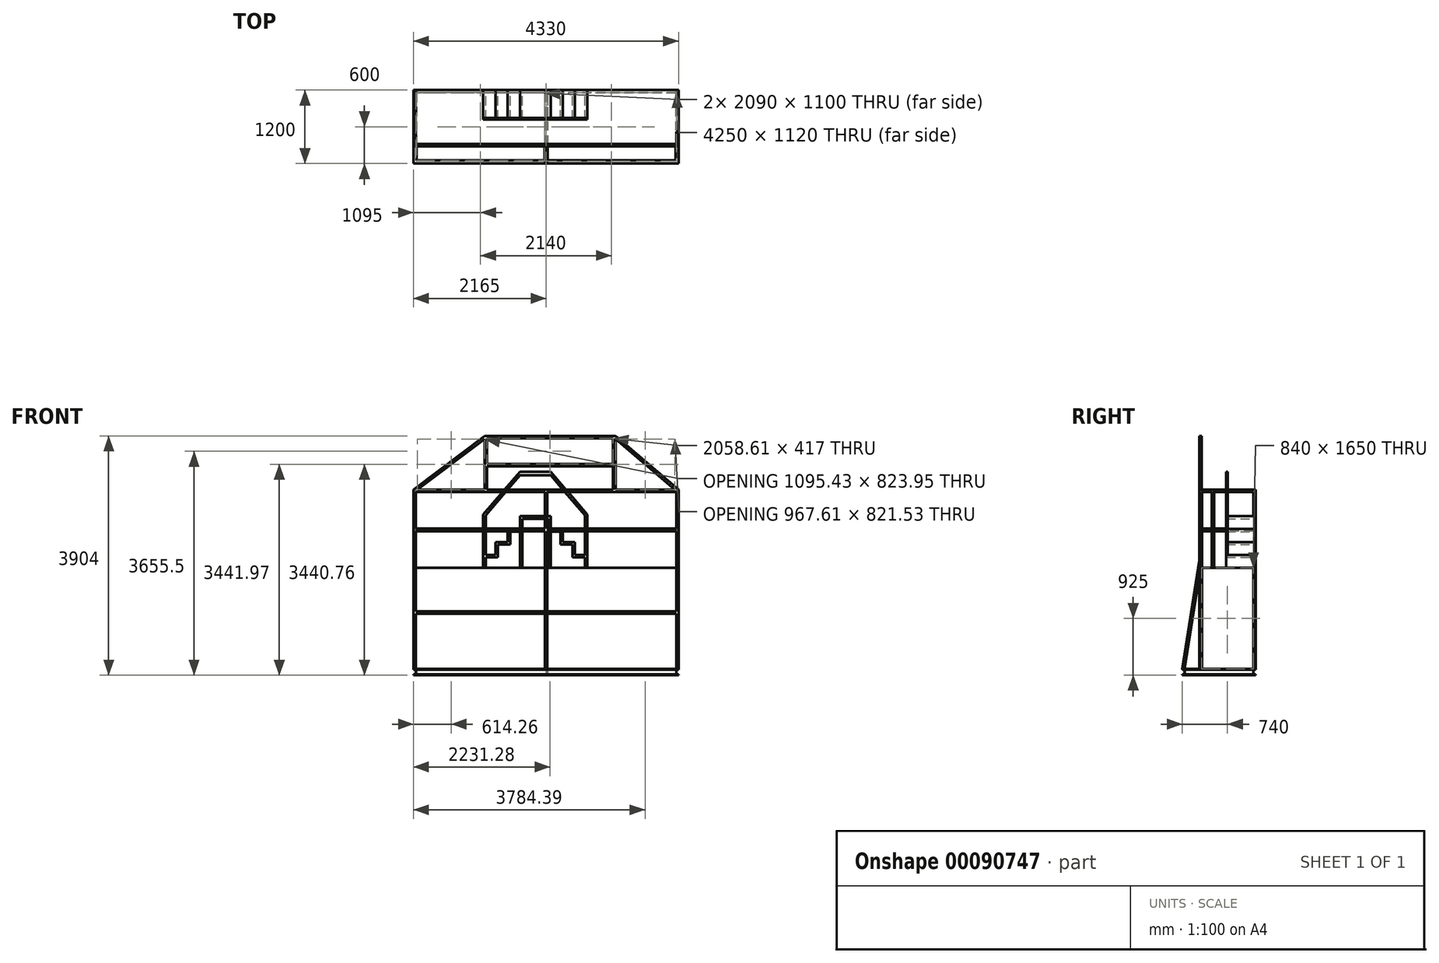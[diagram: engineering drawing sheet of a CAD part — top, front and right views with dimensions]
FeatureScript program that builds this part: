
annotation { "Feature Type Name" : "Feature", "Feature Type Description" : "" }
export const myFeature = defineFeature(function(context is Context, id is Id, definition is map)
    precondition{}
    {
        {
            var Q0;
            Q0=qCreatedBy(makeId("Top.planeOp"),FACE);
            var sketch = newSketch(context, id + "F0", { "sketchPlane" : qUnion([Q0])});
            skLineSegment(sketch, "E0.rect.bottom", {"start": v(2165, 600) * mm, "end": v(-2165, 600) * mm});
            skLineSegment(sketch, "E0.rect.top", {"start": v(2165, -600) * mm, "end": v(-2165, -600) * mm});
            skLineSegment(sketch, "E0.rect.left", {"start": v(2165, 600) * mm, "end": v(2165, -600) * mm});
            skLineSegment(sketch, "E0.rect.right", {"start": v(-2165, 600) * mm, "end": v(-2165, -600) * mm});
            skPoint(sketch, "E0.rect.middle", {"position": v(0, 0) * mm});
            skLineSegment(sketch, "E1.rect.bottom", {"start": v(2115, 550) * mm, "end": v(25, 550) * mm});
            skLineSegment(sketch, "E1.rect.top", {"start": v(2115, -550) * mm, "end": v(25, -550) * mm});
            skLineSegment(sketch, "E1.rect.left", {"start": v(2115, 550) * mm, "end": v(2115, -550) * mm});
            skLineSegment(sketch, "E1.rect.right", {"start": v(-2115, 550) * mm, "end": v(-2115, -550) * mm});
            skLineSegment(sketch, "E2.rect.left", {"start": v(25, 550) * mm, "end": v(25, -550) * mm});
            skLineSegment(sketch, "E2.rect.right", {"start": v(-25, 550) * mm, "end": v(-25, -550) * mm});
            skLineSegment(sketch, "E3.trimOffspring", {"start": v(-25, 550) * mm, "end": v(-2115, 550) * mm});
            skLineSegment(sketch, "E4.trimOffspring", {"start": v(-25, -550) * mm, "end": v(-2115, -550) * mm});
            skSolve(sketch);
        }
        {
            var Q0;
            Q0=makeQuery(id+"F0.imprint","IMPRINT",FACE,{"disambiguationData":[TD([[makeQuery(id+"F0.imprint","IMPRINT",EDGE,{"derivedFrom":sQuery(id+"F0.wireOp",EDGE,"E0.rect.bottom")}),1.0]])]});
            extrude(context, id + "F1", {"entities" : qUnion([Q0]), "depth" : 100 * mm});
        }
        {
            var Q0;
            Q0=makeQuery(id+"F1.opExtrude","SWEPT_FACE",FACE,{"disambiguationData":[OSD([sQuery(id+"F0.wireOp",EDGE,"E0.rect.right")])]});
            var sketch = newSketch(context, id + "F2", { "sketchPlane" : qUnion([Q0])});
            skLineSegment(sketch, "E5.bottom", {"start": v(-600, 90) * mm, "end": v(-560, 90) * mm});
            skLineSegment(sketch, "E5.top", {"start": v(-600, 10) * mm, "end": v(-560, 10) * mm});
            skLineSegment(sketch, "E5.left", {"start": v(-600, 90) * mm, "end": v(-600, 10) * mm});
            skLineSegment(sketch, "E5.right", {"start": v(-560, 90) * mm, "end": v(-560, 10) * mm});
            skLineSegment(sketch, "E6.bottom", {"start": v(600, 90) * mm, "end": v(560, 90) * mm});
            skLineSegment(sketch, "E6.top", {"start": v(600, 10) * mm, "end": v(560, 10) * mm});
            skLineSegment(sketch, "E6.left", {"start": v(600, 90) * mm, "end": v(600, 10) * mm});
            skLineSegment(sketch, "E6.right", {"start": v(560, 90) * mm, "end": v(560, 10) * mm});
            skSolve(sketch);
        }
        {
            var Q0;
            Q0=makeQuery(id+"F2.imprint","IMPRINT",FACE,{"disambiguationData":[TD([[makeQuery(id+"F2.imprint","IMPRINT",EDGE,{"derivedFrom":sQuery(id+"F2.wireOp",EDGE,"E5.bottom")}),-1.0]])]});
            var Q1;
            Q1=makeQuery(id+"F2.imprint","IMPRINT",FACE,{"disambiguationData":[TD([[makeQuery(id+"F2.imprint","IMPRINT",EDGE,{"derivedFrom":sQuery(id+"F2.wireOp",EDGE,"E6.bottom")}),1.0]])]});
            extrude(context, id + "F3", {"entities" : qUnion([Q0, Q1]), "operationType" : NewBodyOperationType.REMOVE, "endBound" : BoundingType.THROUGH_ALL, "oppositeDirection" : true, "depth" : 25 * mm});
        }
        {
            var Q0;
            Q0=makeQuery(id+"F3.boolean.opBoolean","COPY",FACE,{"derivedFrom":makeQuery(id+"F3.opExtrude","SWEPT_FACE",FACE,{"disambiguationData":[OSD([sQuery(id+"F2.wireOp",EDGE,"E6.right")])]})});
            var sketch = newSketch(context, id + "F4", { "sketchPlane" : qUnion([Q0])});
            skLineSegment(sketch, "E7.bottom", {"start": v(2165, 90) * mm, "end": v(2125, 90) * mm});
            skLineSegment(sketch, "E7.top", {"start": v(2165, 10) * mm, "end": v(2125, 10) * mm});
            skLineSegment(sketch, "E7.left", {"start": v(2165, 90) * mm, "end": v(2165, 10) * mm});
            skLineSegment(sketch, "E7.right", {"start": v(2125, 90) * mm, "end": v(2125, 10) * mm});
            skLineSegment(sketch, "E8.bottom", {"start": v(-2165, 90) * mm, "end": v(-2125, 90) * mm});
            skLineSegment(sketch, "E8.top", {"start": v(-2165, 10) * mm, "end": v(-2125, 10) * mm});
            skLineSegment(sketch, "E8.left", {"start": v(-2165, 90) * mm, "end": v(-2165, 10) * mm});
            skLineSegment(sketch, "E8.right", {"start": v(-2125, 90) * mm, "end": v(-2125, 10) * mm});
            skSolve(sketch);
        }
        {
            var Q0;
            Q0=makeQuery(id+"F4.imprint","IMPRINT",FACE,{"disambiguationData":[TD([[makeQuery(id+"F4.imprint","IMPRINT",EDGE,{"derivedFrom":sQuery(id+"F4.wireOp",EDGE,"E7.bottom")}),1.0]])]});
            var Q1;
            Q1=makeQuery(id+"F4.imprint","IMPRINT",FACE,{"disambiguationData":[TD([[makeQuery(id+"F4.imprint","IMPRINT",EDGE,{"derivedFrom":sQuery(id+"F4.wireOp",EDGE,"E8.bottom")}),1.0]])]});
            extrude(context, id + "F5", {"entities" : qUnion([Q0, Q1]), "operationType" : NewBodyOperationType.REMOVE, "endBound" : BoundingType.THROUGH_ALL, "oppositeDirection" : true, "depth" : 25 * mm});
        }
        {
            var Q0;
            Q0=qCreatedBy(makeId("Top.planeOp"),FACE);
            cPlane(context, id + "F6", {"entities" : qUnion([Q0]), "cplaneType" : CPlaneType.OFFSET, "offset" : 1750 * mm, "width" : 150 * mm, "height" : 150 * mm});
        }
        {
            var Q0;
            Q0=qCreatedBy(makeId("Front.planeOp"),FACE);
            var sketch = newSketch(context, id + "F7", { "sketchPlane" : qUnion([Q0])});
            skLineSegment(sketch, "E9.bottom", {"start": v(0, 10) * mm, "end": v(-90, 10) * mm});
            skLineSegment(sketch, "E9.top", {"start": v(0, 90) * mm, "end": v(-90, 90) * mm});
            skLineSegment(sketch, "E9.left", {"start": v(0, 10) * mm, "end": v(0, 90) * mm});
            skLineSegment(sketch, "E9.right", {"start": v(-90, 10) * mm, "end": v(-90, 90) * mm});
            skSolve(sketch);
        }
        {
            var Q0;
            Q0=qSketchRegion(id+"F7",true);
            var Q1;
            Q1=makeQuery(id+"F1.opExtrude","SWEPT_FACE",FACE,{"disambiguationData":[OSD([sQuery(id+"F0.wireOp",EDGE,"E3.trimOffspring")])]});
            var Q2;
            Q2=makeQuery(id+"F1.opExtrude","SWEPT_FACE",FACE,{"disambiguationData":[OSD([sQuery(id+"F0.wireOp",EDGE,"E4.trimOffspring")])]});
            extrude(context, id + "F8", {"entities" : qUnion([Q0]), "operationType" : NewBodyOperationType.REMOVE, "endBound" : BoundingType.UP_TO_SURFACE, "oppositeDirection" : true, "endBoundEntityFace" : qUnion([Q1]), "depth" : 25 * mm, "hasSecondDirection" : true, "secondDirectionBound" : SecondDirectionBoundingType.UP_TO_SURFACE, "secondDirectionOppositeDirection" : false, "secondDirectionBoundEntityFace" : qUnion([Q2]), "secondDirectionDepth" : 25 * mm});
        }
        {
            var Q0;
            Q0=makeQuery(id+"F1.opExtrude","CAP_FACE",FACE,{"disambiguationData":[OSD([sQuery(id+"F0.wireOp",EDGE,"E0.rect.bottom"),sQuery(id+"F0.wireOp",EDGE,"E0.rect.top"),sQuery(id+"F0.wireOp",EDGE,"E0.rect.left"),sQuery(id+"F0.wireOp",EDGE,"E0.rect.right"),sQuery(id+"F0.wireOp",EDGE,"E1.rect.bottom"),sQuery(id+"F0.wireOp",EDGE,"E1.rect.top"),sQuery(id+"F0.wireOp",EDGE,"E1.rect.left"),sQuery(id+"F0.wireOp",EDGE,"E1.rect.right"),sQuery(id+"F0.wireOp",EDGE,"E2.rect.left"),sQuery(id+"F0.wireOp",EDGE,"E2.rect.right"),sQuery(id+"F0.wireOp",EDGE,"E3.trimOffspring"),sQuery(id+"F0.wireOp",EDGE,"E4.trimOffspring")])],"isStart":false});
            var sketch = newSketch(context, id + "F9", { "sketchPlane" : qUnion([Q0])});
            skLineSegment(sketch, "E10.bottom", {"start": v(-2165, 600) * mm, "end": v(-2125, 600) * mm});
            skLineSegment(sketch, "E10.top", {"start": v(-2165, 560) * mm, "end": v(-2125, 560) * mm});
            skLineSegment(sketch, "E10.left", {"start": v(-2165, 600) * mm, "end": v(-2165, 560) * mm});
            skLineSegment(sketch, "E10.right", {"start": v(-2125, 600) * mm, "end": v(-2125, 560) * mm});
            skLineSegment(sketch, "E11.bottom", {"start": v(2165, 600) * mm, "end": v(2125, 600) * mm});
            skLineSegment(sketch, "E11.top", {"start": v(2165, 560) * mm, "end": v(2125, 560) * mm});
            skLineSegment(sketch, "E11.left", {"start": v(2165, 600) * mm, "end": v(2165, 560) * mm});
            skLineSegment(sketch, "E11.right", {"start": v(2125, 600) * mm, "end": v(2125, 560) * mm});
            skLineSegment(sketch, "E12.bottom", {"start": v(-20, 600) * mm, "end": v(20, 600) * mm});
            skLineSegment(sketch, "E12.top", {"start": v(-20, 560) * mm, "end": v(20, 560) * mm});
            skLineSegment(sketch, "E12.left", {"start": v(-20, 600) * mm, "end": v(-20, 560) * mm});
            skLineSegment(sketch, "E12.right", {"start": v(20, 600) * mm, "end": v(20, 560) * mm});
            skLineSegment(sketch, "E13.bottom", {"start": v(-2165, -280) * mm, "end": v(-2125, -280) * mm});
            skLineSegment(sketch, "E13.top", {"start": v(-2165, -320) * mm, "end": v(-2125, -320) * mm});
            skLineSegment(sketch, "E13.left", {"start": v(-2165, -280) * mm, "end": v(-2165, -320) * mm});
            skLineSegment(sketch, "E13.right", {"start": v(-2125, -280) * mm, "end": v(-2125, -320) * mm});
            skLineSegment(sketch, "E14.bottom", {"start": v(-20, -278.81) * mm, "end": v(20, -278.81) * mm});
            skLineSegment(sketch, "E14.top", {"start": v(-20, -320) * mm, "end": v(20, -320) * mm});
            skLineSegment(sketch, "E14.right", {"start": v(20, -278.81) * mm, "end": v(20, -320) * mm});
            skLineSegment(sketch, "E15.bottom", {"start": v(2165, -280) * mm, "end": v(2125, -280) * mm});
            skLineSegment(sketch, "E15.top", {"start": v(2165, -320) * mm, "end": v(2125, -320) * mm});
            skLineSegment(sketch, "E15.left", {"start": v(2165, -280) * mm, "end": v(2165, -320) * mm});
            skLineSegment(sketch, "E15.right", {"start": v(2125, -280) * mm, "end": v(2125, -320) * mm});
            skLineSegment(sketch, "E16", {"start": v(-20, -278.81) * mm, "end": v(-20, -320) * mm});
            skSolve(sketch);
        }
        {
            var Q0;
            Q0=makeQuery(id+"F9.imprint","IMPRINT",FACE,{"disambiguationData":[TD([[makeQuery(id+"F9.imprint","IMPRINT",EDGE,{"derivedFrom":sQuery(id+"F9.wireOp",EDGE,"E14.bottom")}),-1.0]])]});
            var Q1;
            Q1=makeQuery(id+"F9.imprint","IMPRINT",FACE,{"disambiguationData":[TD([[makeQuery(id+"F9.imprint","IMPRINT",EDGE,{"derivedFrom":sQuery(id+"F9.wireOp",EDGE,"E15.bottom")}),1.0]])]});
            var Q2;
            Q2=makeQuery(id+"F9.imprint","IMPRINT",FACE,{"disambiguationData":[TD([[makeQuery(id+"F9.imprint","IMPRINT",EDGE,{"derivedFrom":sQuery(id+"F9.wireOp",EDGE,"E13.bottom")}),-1.0]])]});
            var Q3;
            Q3=makeQuery(id+"F9.imprint","IMPRINT",FACE,{"disambiguationData":[TD([[makeQuery(id+"F9.imprint","IMPRINT",EDGE,{"derivedFrom":sQuery(id+"F9.wireOp",EDGE,"E10.bottom")}),1.0]])]});
            extrude(context, id + "F10", {"entities" : qUnion([Q0, Q1, Q2, Q3]), "operationType" : NewBodyOperationType.ADD, "depth" : 2930 * mm});
        }
        {
            var Q0;
            Q0=qCreatedBy(id+"F6.planeOp",FACE);
            var sketch = newSketch(context, id + "F11", { "sketchPlane" : qUnion([Q0])});
            skLineSegment(sketch, "E17.bottom", {"start": v(-2165, 600) * mm, "end": v(2165, 600) * mm});
            skLineSegment(sketch, "E17.top", {"start": v(-2165, -320) * mm, "end": v(2165, -320) * mm});
            skLineSegment(sketch, "E17.left", {"start": v(-2165, 600) * mm, "end": v(-2165, -320) * mm});
            skLineSegment(sketch, "E17.right", {"start": v(2165, 600) * mm, "end": v(2165, -320) * mm});
            skSolve(sketch);
        }
        {
            var Q0;
            Q0 = qSketchRegion(id + "F11", true);
            extrude(context, id + "F12", {"entities" : qUnion([Q0]), "operationType" : NewBodyOperationType.ADD, "depth" : 4 * mm});
        }
        {
            var Q0;
            Q0 = qSketchRegion(id + "F9", true);
            extrude(context, id + "F13", {"entities" : qUnion([Q0]), "operationType" : NewBodyOperationType.ADD, "depth" : 1650 * mm});
        }
        {
            var Q0;
            {var subQ1=sQuery(id+"F0.wireOp",EDGE,"E0.rect.right");Q0=makeQuery(id+"F12.boolean.opBoolean","MERGE",FACE,{"derivedFrom":[makeQuery(id+"F10.boolean.opBoolean","MERGE",FACE,{"derivedFrom":[makeQuery(id+"F5.boolean.opBoolean","SPLIT",FACE,{"disambiguationData":[TD([makeQuery(id+"F3.boolean.opBoolean","COPY",FACE,{"derivedFrom":makeQuery(id+"F3.opExtrude","SWEPT_FACE",FACE,{"disambiguationData":[OSD([sQuery(id+"F2.wireOp",EDGE,"E5.bottom")])]})})])],"derivedFrom":makeQuery(id+"F1.opExtrude","SWEPT_FACE",FACE,{"disambiguationData":[OSD([subQ1])]})}),makeQuery(id+"F10.opExtrude","SWEPT_FACE",FACE,{"disambiguationData":[OSD([sQuery(id+"F9.wireOp",EDGE,"E10.left")])]}),makeQuery(id+"F10.opExtrude","SWEPT_FACE",FACE,{"disambiguationData":[OSD([sQuery(id+"F9.wireOp",EDGE,"E13.left")])]})]}),makeQuery(id+"F12.opExtrude","SWEPT_FACE",FACE,{"disambiguationData":[OSD([sQuery(id+"F11.wireOp",EDGE,"E17.left")])]})]});}
            var sketch = newSketch(context, id + "F14", { "sketchPlane" : qUnion([Q0])});
            skLineSegment(sketch, "E18.bottom", {"start": v(280, 3030) * mm, "end": v(320, 3030) * mm});
            skLineSegment(sketch, "E18.top", {"start": v(280, 2990) * mm, "end": v(320, 2990) * mm});
            skLineSegment(sketch, "E18.left", {"start": v(280, 3030) * mm, "end": v(280, 2990) * mm});
            skLineSegment(sketch, "E18.right", {"start": v(320, 3030) * mm, "end": v(320, 2990) * mm});
            skLineSegment(sketch, "E19.bottom", {"start": v(-600, 1040) * mm, "end": v(-560, 1040) * mm});
            skLineSegment(sketch, "E19.top", {"start": v(-600, 1000) * mm, "end": v(-560, 1000) * mm});
            skLineSegment(sketch, "E19.left", {"start": v(-600, 1040) * mm, "end": v(-600, 1000) * mm});
            skLineSegment(sketch, "E19.right", {"start": v(-560, 1040) * mm, "end": v(-560, 1000) * mm});
            skLineSegment(sketch, "E20.bottom", {"start": v(280, 1040) * mm, "end": v(320, 1040) * mm});
            skLineSegment(sketch, "E20.top", {"start": v(280, 1000) * mm, "end": v(320, 1000) * mm});
            skLineSegment(sketch, "E20.left", {"start": v(280, 1040) * mm, "end": v(280, 1000) * mm});
            skLineSegment(sketch, "E20.right", {"start": v(320, 1040) * mm, "end": v(320, 1000) * mm});
            skLineSegment(sketch, "E21.bottom", {"start": v(280, 2392) * mm, "end": v(320, 2392) * mm});
            skLineSegment(sketch, "E21.top", {"start": v(280, 2352) * mm, "end": v(320, 2352) * mm});
            skLineSegment(sketch, "E21.left", {"start": v(280, 2392) * mm, "end": v(280, 2352) * mm});
            skLineSegment(sketch, "E21.right", {"start": v(320, 2392) * mm, "end": v(320, 2352) * mm});
            skSolve(sketch);
        }
        {
            var Q0;
            Q0 = qSketchRegion(id + "F14", true);
            extrude(context, id + "F15", {"entities" : qUnion([Q0]), "operationType" : NewBodyOperationType.ADD, "oppositeDirection" : true, "depth" : 4300 * mm});
        }
        {
            var Q0;
            Q0=makeQuery(id+"F15.boolean.opBoolean","MERGE",FACE,{"derivedFrom":[makeQuery(id+"F12.boolean.opBoolean","MERGE",FACE,{"derivedFrom":[makeQuery(id+"F10.opExtrude","SWEPT_FACE",FACE,{"disambiguationData":[OSD([sQuery(id+"F9.wireOp",EDGE,"E13.top")])]}),makeQuery(id+"F10.opExtrude","SWEPT_FACE",FACE,{"disambiguationData":[OSD([sQuery(id+"F9.wireOp",EDGE,"E14.top")])]}),makeQuery(id+"F10.opExtrude","SWEPT_FACE",FACE,{"disambiguationData":[OSD([sQuery(id+"F9.wireOp",EDGE,"E15.top")])]}),makeQuery(id+"F12.opExtrude","SWEPT_FACE",FACE,{"disambiguationData":[OSD([sQuery(id+"F11.wireOp",EDGE,"E17.top")])]})]}),makeQuery(id+"F15.opExtrude","SWEPT_FACE",FACE,{"disambiguationData":[OSD([sQuery(id+"F14.wireOp",EDGE,"E18.right")])]}),makeQuery(id+"F15.opExtrude","SWEPT_FACE",FACE,{"disambiguationData":[OSD([sQuery(id+"F14.wireOp",EDGE,"E20.right")])]}),makeQuery(id+"F15.opExtrude","SWEPT_FACE",FACE,{"disambiguationData":[OSD([sQuery(id+"F14.wireOp",EDGE,"E21.right")])]})]});
            var sketch = newSketch(context, id + "F16", { "sketchPlane" : qUnion([Q0])});
            skLineSegment(sketch, "E22.bottom", {"start": v(-2165, 3030) * mm, "end": v(-2125, 3030) * mm});
            skLineSegment(sketch, "E22.top", {"start": v(-2165, 2990) * mm, "end": v(-2125, 2990) * mm});
            skLineSegment(sketch, "E22.left", {"start": v(-2165, 3030) * mm, "end": v(-2165, 2990) * mm});
            skLineSegment(sketch, "E22.right", {"start": v(-2125, 3030) * mm, "end": v(-2125, 2990) * mm});
            skLineSegment(sketch, "E23.bottom", {"start": v(-2125, 2392) * mm, "end": v(-2165, 2392) * mm});
            skLineSegment(sketch, "E23.top", {"start": v(-2125, 2352) * mm, "end": v(-2165, 2352) * mm});
            skLineSegment(sketch, "E23.left", {"start": v(-2125, 2392) * mm, "end": v(-2125, 2352) * mm});
            skLineSegment(sketch, "E23.right", {"start": v(-2165, 2392) * mm, "end": v(-2165, 2352) * mm});
            skSolve(sketch);
        }
        {
            var Q0;
            Q0=makeQuery(id+"F16.imprint","IMPRINT",FACE,{"disambiguationData":[TD([[makeQuery(id+"F16.imprint","IMPRINT",EDGE,{"derivedFrom":sQuery(id+"F16.wireOp",EDGE,"E22.bottom")}),-1.0]])]});
            var Q1;
            Q1=makeQuery(id+"F16.imprint","IMPRINT",FACE,{"disambiguationData":[TD([[makeQuery(id+"F16.imprint","IMPRINT",EDGE,{"derivedFrom":sQuery(id+"F16.wireOp",EDGE,"E23.bottom")}),1.0]])]});
            extrude(context, id + "F17", {"entities" : qUnion([Q0, Q1]), "operationType" : NewBodyOperationType.ADD, "oppositeDirection" : true, "depth" : 920 * mm});
        }
        {
            var Q0;
            Q0=qCreatedBy(makeId("Right.planeOp"),FACE);
            var sketch = newSketch(context, id + "F18", { "sketchPlane" : qUnion([Q0])});
            skLineSegment(sketch, "E24", {"start": v(-316.25, 1897.77) * mm, "end": v(-599.6, 98.65) * mm});
            skLineSegment(sketch, "E25.0", {"start": v(-286.36, 1830.44) * mm, "end": v(-559.18, 98.21) * mm});
            skLineSegment(sketch, "E26", {"start": v(-559.18, 98.21) * mm, "end": v(-599.6, 98.65) * mm});
            skLineSegment(sketch, "E27", {"start": v(-316.25, 1897.77) * mm, "end": v(-286.36, 1830.44) * mm});
            skSolve(sketch);
        }
        {
            var Q0;
            Q0=makeQuery(id+"F18.imprint","IMPRINT",FACE,{"disambiguationData":[TD([[makeQuery(id+"F18.imprint","IMPRINT",EDGE,{"derivedFrom":sQuery(id+"F18.wireOp",EDGE,"E24")}),1.0]])]});
            extrude(context, id + "F19", {"entities" : qUnion([Q0]), "operationType" : NewBodyOperationType.ADD, "endBound" : BoundingType.SYMMETRIC, "depth" : 40 * mm});
        }
        {
            var Q0;
            Q0=qCreatedBy(makeId("Front.planeOp"),FACE);
            cPlane(context, id + "F20", {"entities" : qUnion([Q0]), "cplaneType" : CPlaneType.OFFSET, "offset" : 600 * mm, "oppositeDirection" : true, "width" : 150 * mm, "height" : 150 * mm});
        }
        {
            var Q0;
            Q0=qCreatedBy(id+"F20.planeOp",FACE);
            var sketch = newSketch(context, id + "F21", { "sketchPlane" : qUnion([Q0])});
            skLineSegment(sketch, "E28", {"start": v(73.97, 1754) * mm, "end": v(73.97, 2594) * mm});
            skLineSegment(sketch, "E29", {"start": v(73.97, 2594) * mm, "end": v(-426.03, 2594) * mm});
            skLineSegment(sketch, "E30", {"start": v(-426.03, 2594) * mm, "end": v(-426.03, 1754) * mm});
            skLineSegment(sketch, "E31", {"start": v(-426.03, 1754) * mm, "end": v(-386.03, 1754) * mm});
            skLineSegment(sketch, "E32", {"start": v(-386.03, 1754) * mm, "end": v(-386.03, 2554) * mm});
            skLineSegment(sketch, "E33", {"start": v(-386.03, 2554) * mm, "end": v(33.97, 2554) * mm});
            skLineSegment(sketch, "E34", {"start": v(33.97, 2554) * mm, "end": v(33.97, 1754) * mm});
            skLineSegment(sketch, "E35", {"start": v(33.97, 1754) * mm, "end": v(73.97, 1754) * mm});
            skLineSegment(sketch, "E36", {"start": v(73.97, 2384) * mm, "end": v(273.97, 2384) * mm});
            skLineSegment(sketch, "E37", {"start": v(273.97, 2384) * mm, "end": v(273.97, 2174) * mm});
            skLineSegment(sketch, "E38", {"start": v(273.97, 2174) * mm, "end": v(473.97, 2174) * mm});
            skLineSegment(sketch, "E39", {"start": v(473.97, 2174) * mm, "end": v(473.97, 1964) * mm});
            skLineSegment(sketch, "E40", {"start": v(473.97, 1964) * mm, "end": v(433.97, 1964) * mm});
            skLineSegment(sketch, "E41", {"start": v(433.97, 1964) * mm, "end": v(433.97, 2134) * mm});
            skLineSegment(sketch, "E42", {"start": v(433.97, 2134) * mm, "end": v(233.97, 2134) * mm});
            skLineSegment(sketch, "E43", {"start": v(233.97, 2134) * mm, "end": v(233.97, 2344) * mm});
            skLineSegment(sketch, "E44", {"start": v(233.97, 2344) * mm, "end": v(73.97, 2344) * mm});
            skLineSegment(sketch, "E45", {"start": v(-176.03, 2594) * mm, "end": v(-176.03, 2051.5) * mm, "construction": true});
            skLineSegment(sketch, "E46.MirrorCS", {"start": v(-586.03, 2344) * mm, "end": v(-426.03, 2344) * mm});
            skLineSegment(sketch, "E47.MirrorCS", {"start": v(-426.03, 2384) * mm, "end": v(-626.03, 2384) * mm});
            skLineSegment(sketch, "E48.MirrorCS", {"start": v(-626.03, 2384) * mm, "end": v(-626.03, 2174) * mm});
            skLineSegment(sketch, "E49.MirrorCS", {"start": v(-786.03, 2134) * mm, "end": v(-586.03, 2134) * mm});
            skLineSegment(sketch, "E50.MirrorCS", {"start": v(-626.03, 2174) * mm, "end": v(-826.03, 2174) * mm});
            skLineSegment(sketch, "E51.MirrorCS", {"start": v(-826.03, 2174) * mm, "end": v(-826.03, 1964) * mm});
            skLineSegment(sketch, "E52.MirrorCS", {"start": v(-786.03, 1964) * mm, "end": v(-786.03, 2134) * mm});
            skLineSegment(sketch, "E53.MirrorCS", {"start": v(-586.03, 2134) * mm, "end": v(-586.03, 2344) * mm});
            skLineSegment(sketch, "E54.MirrorCS", {"start": v(-826.03, 1964) * mm, "end": v(-786.03, 1964) * mm});
            skLineSegment(sketch, "E55", {"start": v(473.97, 1964) * mm, "end": v(673.97, 1964) * mm});
            skLineSegment(sketch, "E56", {"start": v(673.97, 1964) * mm, "end": v(673.97, 1754) * mm});
            skLineSegment(sketch, "E57", {"start": v(673.97, 1754) * mm, "end": v(633.97, 1754) * mm});
            skLineSegment(sketch, "E58", {"start": v(633.97, 1754) * mm, "end": v(633.97, 1924) * mm});
            skLineSegment(sketch, "E59", {"start": v(633.97, 1924) * mm, "end": v(433.97, 1924) * mm});
            skLineSegment(sketch, "E60", {"start": v(433.97, 1924) * mm, "end": v(433.97, 1964) * mm});
            skLineSegment(sketch, "E61.MirrorCS", {"start": v(-986.03, 1924) * mm, "end": v(-786.03, 1924) * mm});
            skLineSegment(sketch, "E62.MirrorCS", {"start": v(-826.03, 1964) * mm, "end": v(-1026.03, 1964) * mm});
            skLineSegment(sketch, "E63.MirrorCS", {"start": v(-1026.03, 1964) * mm, "end": v(-1026.03, 1754) * mm});
            skLineSegment(sketch, "E64.MirrorCS", {"start": v(-986.03, 1754) * mm, "end": v(-986.03, 1924) * mm});
            skLineSegment(sketch, "E65.MirrorCS", {"start": v(-786.03, 1924) * mm, "end": v(-786.03, 1964) * mm});
            skLineSegment(sketch, "E66.MirrorCS", {"start": v(-1026.03, 1754) * mm, "end": v(-986.03, 1754) * mm});
            skSolve(sketch);
        }
        {
            var Q0;
            {var subQ1=sQuery(id+"F21.wireOp",EDGE,"QDDcSzbj-dvXj-XOp7-vtiu-wOcYaTmfimKI");Q0=makeQuery(id+"F21.imprint","IMPRINT",FACE,{"disambiguationData":[TD([[makeQuery(id+"F21.imprint","IMPRINT",EDGE,{"derivedFrom":subQ1}),-1.0]])]});}
            var Q1;
            {var subQ0=sQuery(id+"F21.wireOp",EDGE,"E29");Q1=makeQuery(id+"F21.imprint","IMPRINT",FACE,{"disambiguationData":[TD([[makeQuery(id+"F21.imprint","IMPRINT",EDGE,{"derivedFrom":subQ0}),1.0]])]});}
            var Q2;
            {var subQ1=sQuery(id+"F21.wireOp",EDGE,"Bypho93v-gEm8-qDYy-SaEK-ACIk8DJtcY5p");Q2=makeQuery(id+"F21.imprint","IMPRINT",FACE,{"disambiguationData":[TD([[makeQuery(id+"F21.imprint","IMPRINT",EDGE,{"derivedFrom":subQ1}),1.0]])]});}
            var Q3;
            {var subQ0=sQuery(id+"F21.wireOp",EDGE,"E36");Q3=makeQuery(id+"F21.imprint","IMPRINT",FACE,{"disambiguationData":[TD([[makeQuery(id+"F21.imprint","IMPRINT",EDGE,{"derivedFrom":subQ0}),-1.0]])]});}
            var Q4;
            {var subQ1=sQuery(id+"F21.wireOp",EDGE,"E46.MirrorCS");Q4=makeQuery(id+"F21.imprint","IMPRINT",FACE,{"disambiguationData":[TD([[makeQuery(id+"F21.imprint","IMPRINT",EDGE,{"derivedFrom":subQ1}),1.0]])]});}
            var Q5;
            Q5=makeQuery(id+"F21.imprint","IMPRINT",FACE,{"disambiguationData":[TD([[makeQuery(id+"F21.imprint","IMPRINT",EDGE,{"derivedFrom":sQuery(id+"F21.wireOp",EDGE,"E40")}),1.0]])]});
            var Q6;
            Q6=makeQuery(id+"F21.imprint","IMPRINT",FACE,{"disambiguationData":[TD([[makeQuery(id+"F21.imprint","IMPRINT",EDGE,{"derivedFrom":sQuery(id+"F21.wireOp",EDGE,"E54.MirrorCS")}),-1.0]])]});
            extrude(context, id + "F22", {"entities" : qUnion([Q0, Q1, Q2, Q3, Q4, Q5, Q6]), "operationType" : NewBodyOperationType.ADD, "depth" : 480 * mm});
        }
        {
            var Q0;
            Q0=makeQuery(id+"F15.boolean.opBoolean","MERGE",FACE,{"derivedFrom":[makeQuery(id+"F12.boolean.opBoolean","MERGE",FACE,{"derivedFrom":[makeQuery(id+"F10.opExtrude","SWEPT_FACE",FACE,{"disambiguationData":[OSD([sQuery(id+"F9.wireOp",EDGE,"E13.top")])]}),makeQuery(id+"F10.opExtrude","SWEPT_FACE",FACE,{"disambiguationData":[OSD([sQuery(id+"F9.wireOp",EDGE,"E14.top")])]}),makeQuery(id+"F10.opExtrude","SWEPT_FACE",FACE,{"disambiguationData":[OSD([sQuery(id+"F9.wireOp",EDGE,"E15.top")])]}),makeQuery(id+"F12.opExtrude","SWEPT_FACE",FACE,{"disambiguationData":[OSD([sQuery(id+"F11.wireOp",EDGE,"E17.top")])]})]}),makeQuery(id+"F15.opExtrude","SWEPT_FACE",FACE,{"disambiguationData":[OSD([sQuery(id+"F14.wireOp",EDGE,"E18.right")])]}),makeQuery(id+"F15.opExtrude","SWEPT_FACE",FACE,{"disambiguationData":[OSD([sQuery(id+"F14.wireOp",EDGE,"E20.right")])]}),makeQuery(id+"F15.opExtrude","SWEPT_FACE",FACE,{"disambiguationData":[OSD([sQuery(id+"F14.wireOp",EDGE,"E21.right")])]})]});
            var sketch = newSketch(context, id + "F23", { "sketchPlane" : qUnion([Q0])});
            skLineSegment(sketch, "E67", {"start": v(-1003.02, 3030) * mm, "end": v(-1003.02, 3904) * mm});
            skLineSegment(sketch, "E68", {"start": v(-1003.02, 3904) * mm, "end": v(1135.58, 3904) * mm});
            skLineSegment(sketch, "E69", {"start": v(1135.58, 3904) * mm, "end": v(1135.58, 3030) * mm});
            skLineSegment(sketch, "E70", {"start": v(-1003.02, 3904) * mm, "end": v(-2165, 3030) * mm});
            skLineSegment(sketch, "E71", {"start": v(1135.58, 3904) * mm, "end": v(2165, 3030) * mm});
            skLineSegment(sketch, "E72", {"start": v(-963.02, 3030) * mm, "end": v(-963.02, 3864) * mm});
            skLineSegment(sketch, "E73", {"start": v(-963.02, 3864) * mm, "end": v(1095.58, 3864) * mm});
            skLineSegment(sketch, "E74", {"start": v(1095.58, 3864) * mm, "end": v(1095.58, 3030) * mm});
            skLineSegment(sketch, "E75", {"start": v(-1003.02, 3853.95) * mm, "end": v(-2098.46, 3030) * mm});
            skLineSegment(sketch, "E76", {"start": v(1135.58, 3851.53) * mm, "end": v(2103.2, 3030) * mm});
            skLineSegment(sketch, "E77", {"start": v(-963.02, 3447) * mm, "end": v(1095.58, 3447) * mm});
            skLineSegment(sketch, "E78", {"start": v(-963.02, 3407) * mm, "end": v(1095.58, 3407) * mm});
            skSolve(sketch);
        }
        {
            var Q0;
            {var subQ0=sQuery(id+"F23.wireOp",EDGE,"E70");Q0=makeQuery(id+"F23.imprint","IMPRINT",FACE,{"disambiguationData":[TD([[makeQuery(id+"F23.imprint","IMPRINT",EDGE,{"derivedFrom":subQ0}),1.0]])]});}
            var Q1;
            {var subQ16=sQuery(id+"F23.wireOp",EDGE,"E68");Q1=makeQuery(id+"F23.imprint","IMPRINT",FACE,{"disambiguationData":[TD([[makeQuery(id+"F23.imprint","IMPRINT",EDGE,{"derivedFrom":subQ16}),-1.0]])]});}
            var Q2;
            {var subQ0=sQuery(id+"F23.wireOp",EDGE,"E77");Q2=makeQuery(id+"F23.imprint","IMPRINT",FACE,{"disambiguationData":[TD([[makeQuery(id+"F23.imprint","IMPRINT",EDGE,{"derivedFrom":subQ0}),-1.0]])]});}
            var Q3;
            {var subQ0=sQuery(id+"F23.wireOp",EDGE,"E71");Q3=makeQuery(id+"F23.imprint","IMPRINT",FACE,{"disambiguationData":[TD([[makeQuery(id+"F23.imprint","IMPRINT",EDGE,{"derivedFrom":subQ0}),-1.0]])]});}
            extrude(context, id + "F24", {"entities" : qUnion([Q0, Q1, Q2, Q3]), "operationType" : NewBodyOperationType.ADD, "oppositeDirection" : true, "depth" : 40 * mm});
        }
        {
            var Q0;
            Q0=makeQuery(id+"F12.opExtrude","CAP_FACE",FACE,{"disambiguationData":[OSD([sQuery(id+"F11.wireOp",EDGE,"E17.bottom"),sQuery(id+"F11.wireOp",EDGE,"E17.top"),sQuery(id+"F11.wireOp",EDGE,"E17.left"),sQuery(id+"F11.wireOp",EDGE,"E17.right")])],"isStart":false});
            var sketch = newSketch(context, id + "F25", { "sketchPlane" : qUnion([Q0])});
            skLineSegment(sketch, "E79.bottom", {"start": v(2165, -80) * mm, "end": v(2125, -80) * mm});
            skLineSegment(sketch, "E79.top", {"start": v(2165, -120) * mm, "end": v(2125, -120) * mm});
            skLineSegment(sketch, "E79.left", {"start": v(2165, -80) * mm, "end": v(2165, -120) * mm});
            skLineSegment(sketch, "E79.right", {"start": v(2125, -80) * mm, "end": v(2125, -120) * mm});
            skSolve(sketch);
        }
        {
            var Q0;
            Q0=makeQuery(id+"F25.imprint","IMPRINT",FACE,{"disambiguationData":[TD([[makeQuery(id+"F25.imprint","IMPRINT",EDGE,{"derivedFrom":sQuery(id+"F25.wireOp",EDGE,"E79.bottom")}),1.0]])]});
            extrude(context, id + "F26", {"entities" : qUnion([Q0]), "operationType" : NewBodyOperationType.ADD, "depth" : 1250 * mm});
        }
        {
            var Q0;
            {var subQ0=sQuery(id+"F14.wireOp",EDGE,"E18.right");var subQ1=sQuery(id+"F9.wireOp",EDGE,"E15.top");var subQ2=sQuery(id+"F9.wireOp",EDGE,"E14.top");var subQ3=sQuery(id+"F9.wireOp",EDGE,"E13.top");Q0=makeQuery(id+"F24.boolean.opBoolean","MERGE",FACE,{"derivedFrom":[makeQuery(id+"F15.boolean.opBoolean","MERGE",FACE,{"derivedFrom":[makeQuery(id+"F12.boolean.opBoolean","MERGE",FACE,{"derivedFrom":[makeQuery(id+"F10.opExtrude","SWEPT_FACE",FACE,{"disambiguationData":[OSD([subQ3])]}),makeQuery(id+"F10.opExtrude","SWEPT_FACE",FACE,{"disambiguationData":[OSD([subQ2])]}),makeQuery(id+"F10.opExtrude","SWEPT_FACE",FACE,{"disambiguationData":[OSD([subQ1])]}),makeQuery(id+"F12.opExtrude","SWEPT_FACE",FACE,{"disambiguationData":[OSD([sQuery(id+"F11.wireOp",EDGE,"E17.top")])]})]}),makeQuery(id+"F15.opExtrude","SWEPT_FACE",FACE,{"disambiguationData":[OSD([subQ0])]}),makeQuery(id+"F15.opExtrude","SWEPT_FACE",FACE,{"disambiguationData":[OSD([sQuery(id+"F14.wireOp",EDGE,"E20.right")])]}),makeQuery(id+"F15.opExtrude","SWEPT_FACE",FACE,{"disambiguationData":[OSD([sQuery(id+"F14.wireOp",EDGE,"E21.right")])]})]}),makeQuery(id+"F24.opExtrude","CAP_FACE",FACE,{"disambiguationData":[OSD([subQ3,subQ2,subQ1,sQuery(id+"F14.wireOp",EDGE,"E18.bottom"),subQ0,sQuery(id+"F23.wireOp",EDGE,"E67"),sQuery(id+"F23.wireOp",EDGE,"E68"),sQuery(id+"F23.wireOp",EDGE,"E69"),sQuery(id+"F23.wireOp",EDGE,"E70"),sQuery(id+"F23.wireOp",EDGE,"E71"),sQuery(id+"F23.wireOp",EDGE,"E72"),sQuery(id+"F23.wireOp",EDGE,"E73"),sQuery(id+"F23.wireOp",EDGE,"E74"),sQuery(id+"F23.wireOp",EDGE,"E75"),sQuery(id+"F23.wireOp",EDGE,"E76"),sQuery(id+"F23.wireOp",EDGE,"E77"),sQuery(id+"F23.wireOp",EDGE,"E78")])],"isStart":true})]});}
            var sketch = newSketch(context, id + "F27", { "sketchPlane" : qUnion([Q0])});
            skLineSegment(sketch, "E80.bottom", {"start": v(2125, 2990) * mm, "end": v(2165, 2990) * mm});
            skLineSegment(sketch, "E80.top", {"start": v(2125, 3030) * mm, "end": v(2165, 3030) * mm});
            skLineSegment(sketch, "E80.left", {"start": v(2125, 2990) * mm, "end": v(2125, 3030) * mm});
            skLineSegment(sketch, "E80.right", {"start": v(2165, 2990) * mm, "end": v(2165, 3030) * mm});
            skSolve(sketch);
        }
        {
            var Q0;
            Q0=makeQuery(id+"F27.imprint","IMPRINT",FACE,{"disambiguationData":[TD([[makeQuery(id+"F27.imprint","IMPRINT",EDGE,{"derivedFrom":sQuery(id+"F27.wireOp",EDGE,"E80.bottom")}),1.0]])]});
            extrude(context, id + "F28", {"entities" : qUnion([Q0]), "operationType" : NewBodyOperationType.ADD, "oppositeDirection" : true, "depth" : 240 * mm});
        }
        {
            var Q0;
            Q0=makeQuery(id+"F22.opExtrude","CAP_FACE",FACE,{"disambiguationData":[OSD([sQuery(id+"F21.wireOp",EDGE,"E28"),sQuery(id+"F21.wireOp",EDGE,"E29"),sQuery(id+"F21.wireOp",EDGE,"E30"),sQuery(id+"F21.wireOp",EDGE,"E31"),sQuery(id+"F21.wireOp",EDGE,"E32"),sQuery(id+"F21.wireOp",EDGE,"E33"),sQuery(id+"F21.wireOp",EDGE,"E34"),sQuery(id+"F21.wireOp",EDGE,"E35"),sQuery(id+"F21.wireOp",EDGE,"E36"),sQuery(id+"F21.wireOp",EDGE,"E37"),sQuery(id+"F21.wireOp",EDGE,"E38"),sQuery(id+"F21.wireOp",EDGE,"E39"),sQuery(id+"F21.wireOp",EDGE,"E41"),sQuery(id+"F21.wireOp",EDGE,"E42"),sQuery(id+"F21.wireOp",EDGE,"E43"),sQuery(id+"F21.wireOp",EDGE,"E44"),sQuery(id+"F21.wireOp",EDGE,"E46.MirrorCS"),sQuery(id+"F21.wireOp",EDGE,"E47.MirrorCS"),sQuery(id+"F21.wireOp",EDGE,"E48.MirrorCS"),sQuery(id+"F21.wireOp",EDGE,"E49.MirrorCS"),sQuery(id+"F21.wireOp",EDGE,"E50.MirrorCS"),sQuery(id+"F21.wireOp",EDGE,"E51.MirrorCS"),sQuery(id+"F21.wireOp",EDGE,"E52.MirrorCS"),sQuery(id+"F21.wireOp",EDGE,"E53.MirrorCS"),sQuery(id+"F21.wireOp",EDGE,"E55"),sQuery(id+"F21.wireOp",EDGE,"E56"),sQuery(id+"F21.wireOp",EDGE,"E57"),sQuery(id+"F21.wireOp",EDGE,"E58"),sQuery(id+"F21.wireOp",EDGE,"E59"),sQuery(id+"F21.wireOp",EDGE,"E60"),sQuery(id+"F21.wireOp",EDGE,"E61.MirrorCS"),sQuery(id+"F21.wireOp",EDGE,"E62.MirrorCS"),sQuery(id+"F21.wireOp",EDGE,"E63.MirrorCS"),sQuery(id+"F21.wireOp",EDGE,"E64.MirrorCS"),sQuery(id+"F21.wireOp",EDGE,"E65.MirrorCS"),sQuery(id+"F21.wireOp",EDGE,"E66.MirrorCS")])],"isStart":false});
            var sketch = newSketch(context, id + "F29", { "sketchPlane" : qUnion([Q0])});
            skPoint(sketch, "E81.endSnap0", {"position": v(73.97, 2489) * mm});
            skLineSegment(sketch, "E82", {"start": v(-1026.03, 1964) * mm, "end": v(-986.03, 1964) * mm});
            skLineSegment(sketch, "E83", {"start": v(633.97, 1964) * mm, "end": v(673.97, 1964) * mm});
            skLineSegment(sketch, "E84", {"start": v(-176.03, 2594) * mm, "end": v(-176.03, 3602.47) * mm, "construction": true});
            skLineSegment(sketch, "E85", {"start": v(73.97, 2594) * mm, "end": v(73.97, 3668.56) * mm, "construction": true});
            skLineSegment(sketch, "E86", {"start": v(-426.03, 2594) * mm, "end": v(-426.03, 3603.3) * mm, "construction": true});
            skLineSegment(sketch, "E87", {"start": v(-1026.03, 1964) * mm, "end": v(-1026.03, 2623.44) * mm});
            skLineSegment(sketch, "E88", {"start": v(-1026.03, 2623.44) * mm, "end": v(-426.03, 3323.56) * mm});
            skLineSegment(sketch, "E89", {"start": v(-426.03, 3323.56) * mm, "end": v(-176.03, 3323.56) * mm});
            skLineSegment(sketch, "E90", {"start": v(-176.03, 3323.56) * mm, "end": v(-176.03, 3262.1) * mm});
            skLineSegment(sketch, "E91", {"start": v(-176.03, 3262.1) * mm, "end": v(-426.03, 3262.1) * mm});
            skLineSegment(sketch, "E92", {"start": v(-426.03, 3262.1) * mm, "end": v(-986.03, 2608.64) * mm});
            skLineSegment(sketch, "E93", {"start": v(-986.03, 2608.64) * mm, "end": v(-986.03, 1964) * mm});
            skLineSegment(sketch, "E94.MirrorCS", {"start": v(-176.03, 3262.1) * mm, "end": v(73.97, 3262.1) * mm});
            skLineSegment(sketch, "E95.MirrorCS", {"start": v(73.97, 3323.56) * mm, "end": v(-176.03, 3323.56) * mm});
            skLineSegment(sketch, "E96.MirrorCS", {"start": v(673.97, 2623.44) * mm, "end": v(73.97, 3323.56) * mm});
            skLineSegment(sketch, "E97.MirrorCS", {"start": v(73.97, 3262.1) * mm, "end": v(633.97, 2608.64) * mm});
            skLineSegment(sketch, "E98.MirrorCS", {"start": v(673.97, 1964) * mm, "end": v(673.97, 2623.44) * mm});
            skLineSegment(sketch, "E99.MirrorCS", {"start": v(633.97, 2608.64) * mm, "end": v(633.97, 1964) * mm});
            skSolve(sketch);
        }
        {
            var Q0;
            Q0=makeQuery(id+"F29.imprint","IMPRINT",FACE,{"disambiguationData":[TD([[makeQuery(id+"F29.imprint","IMPRINT",EDGE,{"derivedFrom":sQuery(id+"F29.wireOp",EDGE,"kj9H4cpo-WZYA-L58w-gy0i-ARGhy10xVLZ4")}),-1.0]])]});
            var Q1;
            Q1=makeQuery(id+"F29.imprint","IMPRINT",FACE,{"disambiguationData":[TD([[makeQuery(id+"F29.imprint","IMPRINT",EDGE,{"derivedFrom":sQuery(id+"F29.wireOp",EDGE,"E82")}),-1.0]])]});
            var Q2;
            Q2=makeQuery(id+"F29.imprint","IMPRINT",FACE,{"disambiguationData":[TD([[makeQuery(id+"F29.imprint","IMPRINT",EDGE,{"derivedFrom":sQuery(id+"F29.wireOp",EDGE,"E83")}),1.0]])]});
            extrude(context, id + "F30", {"entities" : qUnion([Q0, Q1, Q2]), "operationType" : NewBodyOperationType.ADD, "oppositeDirection" : true, "depth" : 25 * mm});
        }
    });
